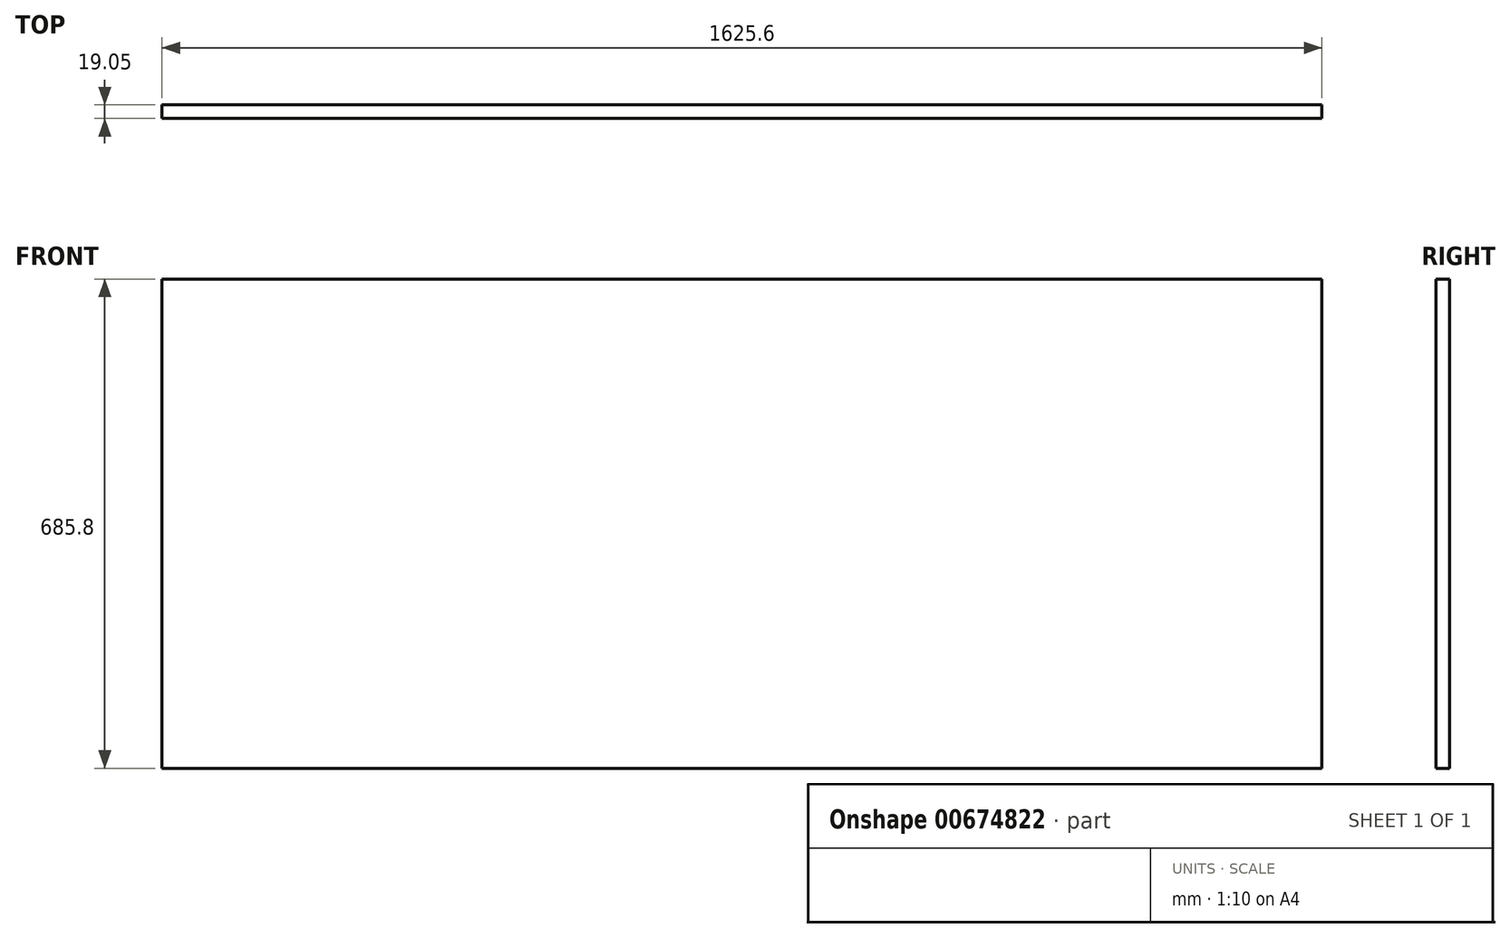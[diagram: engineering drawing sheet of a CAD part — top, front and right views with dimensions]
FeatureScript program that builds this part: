
annotation { "Feature Type Name" : "Feature", "Feature Type Description" : "" }
export const myFeature = defineFeature(function(context is Context, id is Id, definition is map)
    precondition{}
    {
        {
            var Q0;
            Q0=qCreatedBy(makeId("Front.planeOp"),FACE);
            var sketch = newSketch(context, id + "F0", { "sketchPlane" : qUnion([Q0])});
            skLineSegment(sketch, "E0.bottom", {"start": v(-812.8, 342.9) * mm, "end": v(812.8, 342.9) * mm});
            skLineSegment(sketch, "E0.top", {"start": v(-812.8, -342.9) * mm, "end": v(812.8, -342.9) * mm});
            skLineSegment(sketch, "E0.left", {"start": v(-812.8, 342.9) * mm, "end": v(-812.8, -342.9) * mm});
            skLineSegment(sketch, "E0.right", {"start": v(812.8, 342.9) * mm, "end": v(812.8, -342.9) * mm});
            skPoint(sketch, "E0.middle", {"position": v(0, 0) * mm});
            skSolve(sketch);
        }
        {
            var Q0;
            Q0=makeQuery(id+"F0.imprint","IMPRINT",FACE,{"disambiguationData":[TD([[makeQuery(id+"F0.imprint","IMPRINT",EDGE,{"derivedFrom":sQuery(id+"F0.wireOp",EDGE,"E0.bottom")}),-1.0]])]});
            extrude(context, id + "F1", {"entities" : qUnion([Q0]), "depth" : 19.05 * mm, "offsetDistance" : 25.4 * mm});
        }
    });
